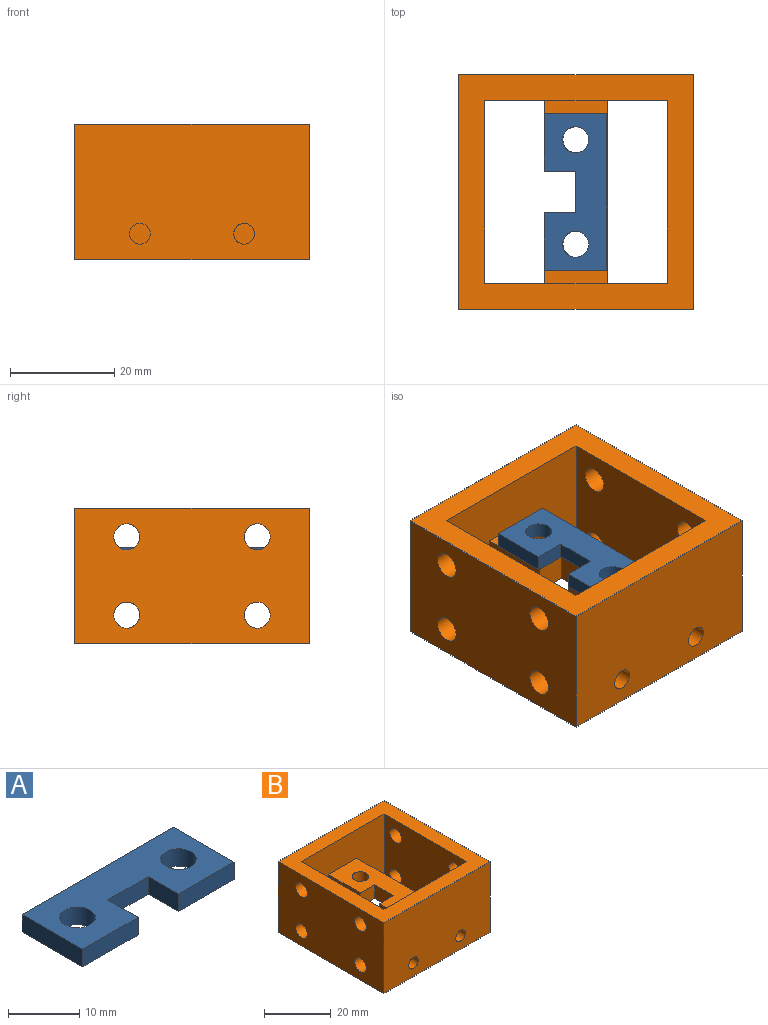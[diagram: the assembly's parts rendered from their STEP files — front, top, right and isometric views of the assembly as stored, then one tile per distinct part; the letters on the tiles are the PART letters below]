
ASSEMBLY  parts=2 mates=1
PART A: 12 faces, bbox 30x12x3 mm
  f0: plane 11x3mm, normal (0,-1,0), area 33mm2, adj f1,f8,f10,f11
  f1: plane 12x3mm, normal (1,0,0), area 36mm2, adj f0,f2,f10,f11
  f2: plane 30x3mm, normal (0,1,0), area 90mm2, adj f1,f3,f10,f11
  f3: plane 12x3mm, normal (-1,0,0), area 36mm2, adj f2,f4,f10,f11
  f4: plane 11x3mm, normal (0,-1,0), area 33mm2, adj f3,f5,f10,f11
  f5: plane 6x3mm, normal (1,0,0), area 18mm2, adj f4,f6,f10,f11
  f6: plane 8x3mm, normal (0,-1,0), area 24mm2, adj f5,f8,f10,f11
  f7: cylinder r=2.5mm len=5mm, axis (0,0,-1), area 47.1mm2, adj f10,f11
  f8: plane 6x3mm, normal (-1,0,0), area 18mm2, adj f0,f6,f10,f11
  f9: cylinder r=2.5mm len=5mm, axis (0,0,-1), area 47.1mm2, adj f10,f11
  f10: plane 30x12mm, normal (0,0,1), area 272.7mm2, adj f0,f1,f2,f3,f4,f5,f6,f7
  f11: plane 30x12mm, normal (0,0,-1), area 272.7mm2, adj f0,f1,f2,f3,f4,f5,f6,f7
PART B: 30 faces, bbox 45x45x26 mm
  f0: plane 13.5x5mm, normal (-1,0,0), area 67.5mm2, adj f1,f2,f4,f27
  f1: plane 35x12mm, normal (0,0,1), area 332.7mm2, adj f0,f3,f4,f23,f24,f25,f26,f27
  f2: plane 35x12mm, normal (0,0,-1), area 332.7mm2, adj f0,f3,f4,f23,f24,f25,f26,f27
  f3: plane 35x26mm, normal (0,-1,0), area 850mm2, adj f1,f2,f5,f6,f11,f12,f23,f24
  f4: plane 35x26mm, normal (0,1,0), area 824.9mm2, adj f0,f1,f2,f5,f6,f11,f12,f21
  f5: plane 45x45mm, normal (0,0,1), area 800mm2, adj f3,f4,f7,f8,f9,f10,f11,f12
  f6: plane 45x45mm, normal (0,0,-1), area 800mm2, adj f3,f4,f7,f8,f9,f10,f11,f12
  f7: plane 45x26mm, normal (1,0,0), area 1091.5mm2, adj f5,f6,f8,f10,f14,f16,f18,f20
  f8: plane 45x26mm, normal (0,1,0), area 1170mm2, adj f5,f6,f7,f9
  f9: plane 45x26mm, normal (-1,0,0), area 1091.5mm2, adj f5,f6,f8,f10,f13,f15,f17,f19
  f10: plane 45x26mm, normal (0,-1,0), area 1144.9mm2, adj f5,f6,f7,f9,f21,f22
  f11: plane 35x26mm, normal (-1,0,0), area 831.5mm2, adj f3,f4,f5,f6,f14,f16,f18,f20
  f12: plane 35x26mm, normal (1,0,0), area 831.5mm2, adj f3,f4,f5,f6,f13,f15,f17,f19
  f13: cylinder r=2.5mm len=5mm, axis (-1,0,0), area 78.5mm2, adj f9,f12
  f14: cylinder r=2.5mm len=5mm, axis (-1,0,0), area 78.5mm2, adj f7,f11
  f15: cylinder r=2.5mm len=5mm, axis (-1,0,0), area 78.5mm2, adj f9,f12
  f16: cylinder r=2.5mm len=5mm, axis (-1,0,0), area 78.5mm2, adj f7,f11
  f17: cylinder r=2.5mm len=5mm, axis (-1,0,0), area 78.5mm2, adj f9,f12
  f18: cylinder r=2.5mm len=5mm, axis (-1,0,0), area 78.5mm2, adj f7,f11
  f19: cylinder r=2.5mm len=5mm, axis (-1,0,0), area 78.5mm2, adj f9,f12
  f20: cylinder r=2.5mm len=5mm, axis (-1,0,0), area 78.5mm2, adj f7,f11
  f21: cylinder r=2mm len=5mm, axis (0,-1,0), area 62.8mm2, adj f4,f10
  f22: cylinder r=2mm len=5mm, axis (0,-1,0), area 62.8mm2, adj f4,f10
  f23: plane 35x5mm, normal (1,0,0), area 175mm2, adj f1,f2,f3,f4
  f24: plane 13.5x5mm, normal (-1,0,0), area 67.5mm2, adj f1,f2,f3,f25
  f25: plane 6x5mm, normal (0,-1,0), area 30mm2, adj f1,f2,f24,f26
  f26: plane 8x5mm, normal (-1,0,0), area 40mm2, adj f1,f2,f25,f27
  f27: plane 6x5mm, normal (0,1,0), area 30mm2, adj f0,f1,f2,f26
  f28: cylinder r=2.5mm len=5mm, axis (0,0,1), area 78.5mm2, adj f1,f2
  f29: cylinder r=2.5mm len=5mm, axis (0,0,1), area 78.5mm2, adj f1,f2
PLACE A rot(axis=(0,0,-1),90deg) t=(-9.69,5.72,61.12)mm
PLACE B t=(-9.59,5.72,57.12)mm
MATE planar A.f11 <-> B.f1  axis (0,0,-1) through (-9.16,5.72,59.62)mm
